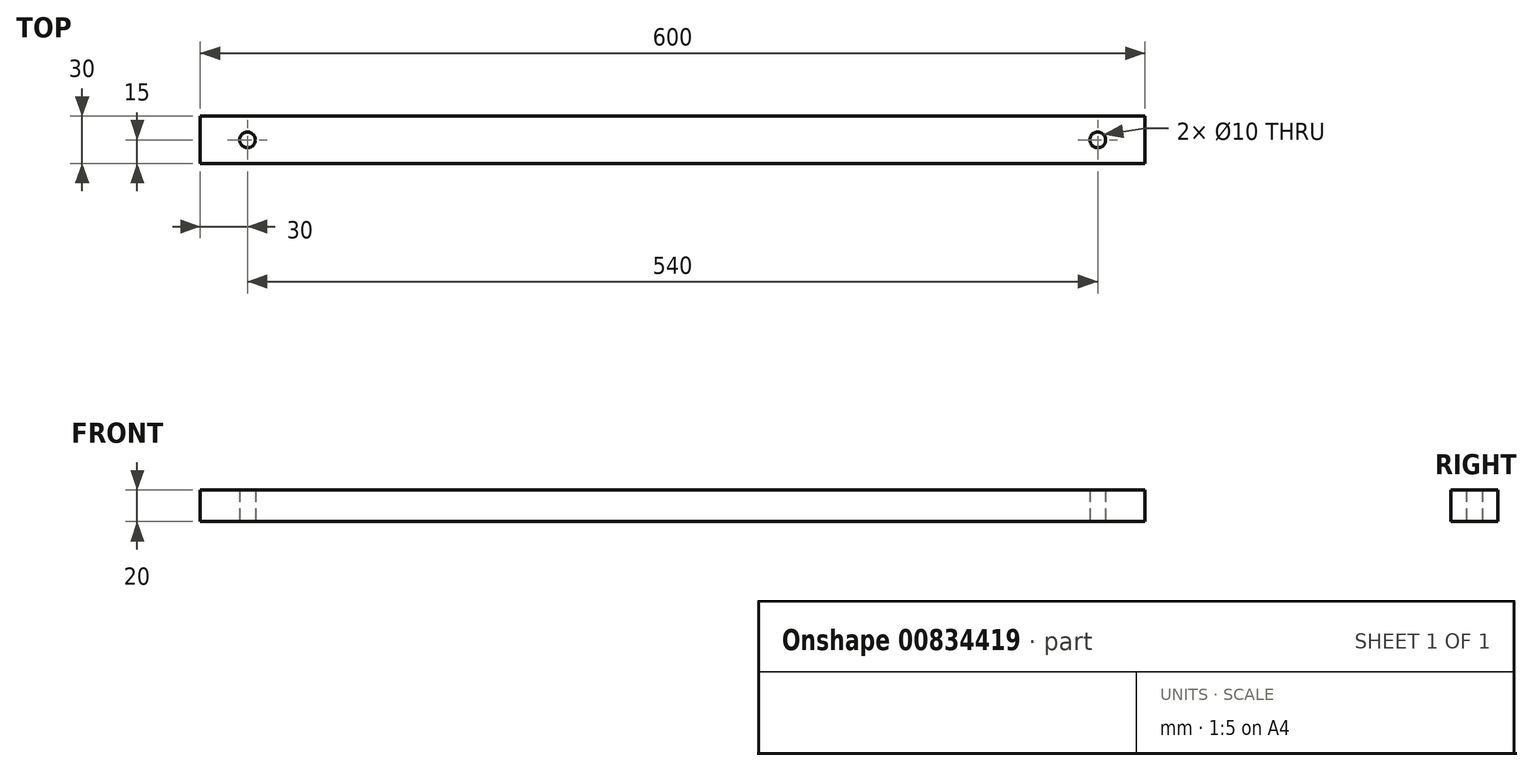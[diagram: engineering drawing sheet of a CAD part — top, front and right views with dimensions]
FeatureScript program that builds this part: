
annotation { "Feature Type Name" : "Feature", "Feature Type Description" : "" }
export const myFeature = defineFeature(function(context is Context, id is Id, definition is map)
    precondition{}
    {
        {
            var Q0;
            Q0=qCreatedBy(makeId("Top.planeOp"),FACE);
            var sketch = newSketch(context, id + "F0", { "sketchPlane" : qUnion([Q0])});
            skLineSegment(sketch, "E0.bottom", {"start": v(-300, 15) * mm, "end": v(300, 15) * mm});
            skLineSegment(sketch, "E0.top", {"start": v(-300, -15) * mm, "end": v(300, -15) * mm});
            skLineSegment(sketch, "E0.left", {"start": v(-300, 15) * mm, "end": v(-300, -15) * mm});
            skLineSegment(sketch, "E0.right", {"start": v(300, 15) * mm, "end": v(300, -15) * mm});
            skPoint(sketch, "E0.middle", {"position": v(0, 0) * mm});
            skCircle(sketch, "E1", {"center": v(270, 0) * mm, "radius": 5 * mm});
            skPoint(sketch, "E1.centerSnap0", {"position": v(300, 0) * mm});
            skCircle(sketch, "E2", {"center": v(-270, 0) * mm, "radius": 5 * mm});
            skSolve(sketch);
        }
        {
            var Q0;
            Q0 = qSketchRegion(id + "F0", true);
            extrude(context, id + "F1", {"entities" : qUnion([Q0]), "depth" : 20 * mm, "offsetDistance" : 25 * mm});
        }
    });
